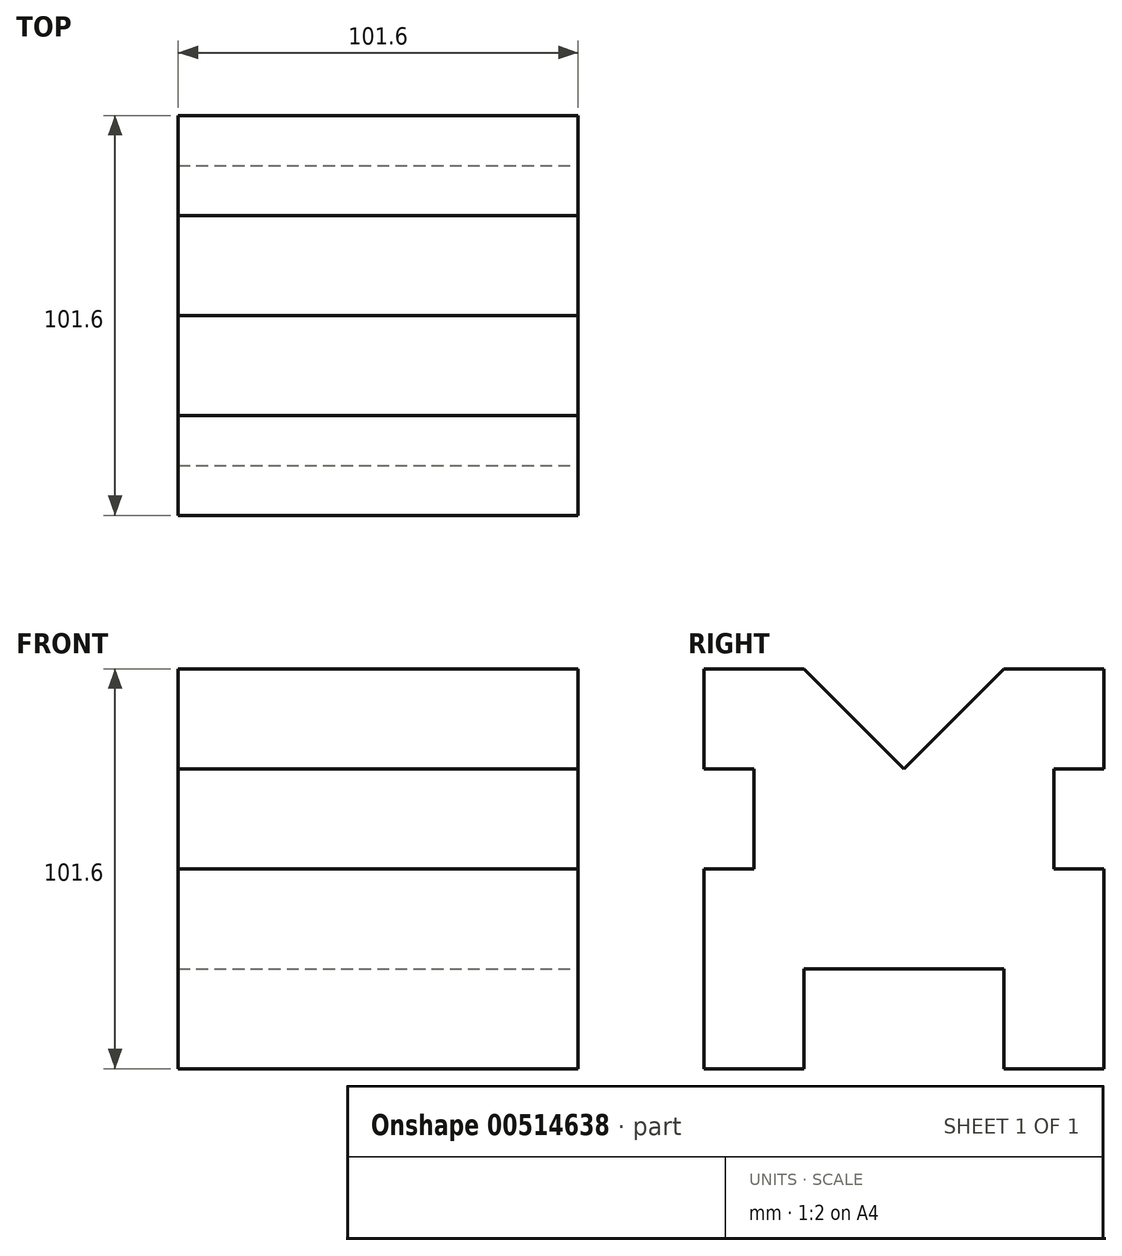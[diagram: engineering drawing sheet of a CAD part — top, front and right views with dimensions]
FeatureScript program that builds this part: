
annotation { "Feature Type Name" : "Feature", "Feature Type Description" : "" }
export const myFeature = defineFeature(function(context is Context, id is Id, definition is map)
    precondition{}
    {
        {
            var Q0;
            Q0=qCreatedBy(makeId("Right.planeOp"),FACE);
            var sketch = newSketch(context, id + "F0", { "sketchPlane" : qUnion([Q0])});
            skLineSegment(sketch, "E0", {"start": v(0, 0) * mm, "end": v(-25.4, 0) * mm});
            skLineSegment(sketch, "E1", {"start": v(-25.4, 0) * mm, "end": v(-25.4, 25.4) * mm});
            skLineSegment(sketch, "E2", {"start": v(-25.4, 25.4) * mm, "end": v(-76.2, 25.4) * mm});
            skLineSegment(sketch, "E3", {"start": v(-76.2, 25.4) * mm, "end": v(-76.2, 0) * mm});
            skLineSegment(sketch, "E4", {"start": v(-76.2, 0) * mm, "end": v(-101.6, 0) * mm});
            skLineSegment(sketch, "E5", {"start": v(-101.6, 0) * mm, "end": v(-101.6, 50.8) * mm});
            skLineSegment(sketch, "E6", {"start": v(-101.6, 50.8) * mm, "end": v(-88.9, 50.8) * mm});
            skLineSegment(sketch, "E7", {"start": v(-88.9, 50.8) * mm, "end": v(-88.9, 76.2) * mm});
            skLineSegment(sketch, "E8", {"start": v(-88.9, 76.2) * mm, "end": v(-101.6, 76.2) * mm});
            skLineSegment(sketch, "E9", {"start": v(-101.6, 76.2) * mm, "end": v(-101.6, 101.6) * mm});
            skLineSegment(sketch, "E10", {"start": v(-101.6, 101.6) * mm, "end": v(-76.2, 101.6) * mm});
            skLineSegment(sketch, "E11", {"start": v(0, 0) * mm, "end": v(0, 50.8) * mm});
            skLineSegment(sketch, "E12", {"start": v(0, 50.8) * mm, "end": v(-12.7, 50.8) * mm});
            skLineSegment(sketch, "E13", {"start": v(-12.7, 50.8) * mm, "end": v(-12.7, 76.2) * mm});
            skLineSegment(sketch, "E14", {"start": v(-12.7, 76.2) * mm, "end": v(0, 76.2) * mm});
            skLineSegment(sketch, "E15", {"start": v(0, 76.2) * mm, "end": v(0, 101.6) * mm});
            skLineSegment(sketch, "E16", {"start": v(0, 101.6) * mm, "end": v(-25.4, 101.6) * mm});
            skLineSegment(sketch, "E17", {"start": v(-25.4, 101.6) * mm, "end": v(-50.8, 76.2) * mm});
            skPoint(sketch, "E17.endSnap0", {"position": v(-50.8, 25.4) * mm});
            skLineSegment(sketch, "E18", {"start": v(-50.8, 76.2) * mm, "end": v(-76.2, 101.6) * mm});
            skSolve(sketch);
        }
        {
            var Q0;
            Q0 = qSketchRegion(id + "F0", true);
            extrude(context, id + "F1", {"entities" : qUnion([Q0]), "oppositeDirection" : true, "depth" : 101.6 * mm, "offsetDistance" : 25.4 * mm});
        }
    });
